FCSTD DOCUMENT  (FreeCAD 0.19R24291 (Git))
Label: P11 isometric
License: All rights reserved
LicenseURL: http://en.wikipedia.org/wiki/All_rights_reserved
objects: Part::Part2DObjectPython×25, App::FeaturePython×9
note: 25 computed .brp shape members not serialized (recipe doc carries the construction recipe); baked Part::Feature solids carry a one-line shape summary decoded from their .brp

FEATURE [Part::Part2DObjectPython] Line001  # Draft 2D object (typed FeaturePython)
  Area = 0
  ChamferSize = 0
  Closed = false
  End = (-15,0,0)
  FilletRadius = 0
  Length = 22.9544
  MakeFace = false
  Points = (2) [(7.95439,0,0),(-15,0,0)]
  Start = (7.95439,0,0)
  Subdivisions = 0
FEATURE [Part::Part2DObjectPython] Line003  # Draft 2D object (typed FeaturePython)
  Area = 0
  ChamferSize = 0
  Closed = false
  End = (-7.07107,7.07107,0)
  FilletRadius = 0
  Length = 10
  MakeFace = false
  Points = (2) [(0,0,0),(-7.07107,7.07107,0)]
  Start = (0,0,0)
  Subdivisions = 0
FEATURE [Part::Part2DObjectPython] Line004  # Draft 2D object (typed FeaturePython)
  Area = 0
  ChamferSize = 0
  Closed = false
  End = (-29.1421,14.1421,0)
  FilletRadius = 0
  Length = 20
  MakeFace = false
  Placement = pos=(-15,-1e-15,0) rot=(0,0,1;0rad)
  Points = (2) [(0,0,0),(-14.1421,14.1421,0)]
  Start = (-15,-1e-15,0)
  Subdivisions = 0
FEATURE [Part::Part2DObjectPython] Line005  # Draft 2D object (typed FeaturePython)
  Area = 0
  ChamferSize = 0
  Closed = false
  End = (-19.1421,14.1421,0)
  FilletRadius = 0
  Length = 10
  MakeFace = false
  Placement = pos=(-29.1421,14.1421,0) rot=(0,0,1;0rad)
  Points = (2) [(0,0,0),(10,-1.24345e-14,0)]
  Start = (-29.1421,14.1421,0)
  Subdivisions = 0
FEATURE [Part::Part2DObjectPython] Line006  # Draft 2D object (typed FeaturePython)
  Area = 0
  ChamferSize = 0
  Closed = false
  End = (-12.0711,7.07107,0)
  FilletRadius = 0
  Length = 10
  MakeFace = false
  Placement = pos=(-19.1421,14.1421,0) rot=(0,0,1;0rad)
  Points = (2) [(0,0,0),(7.07107,-7.07107,0)]
  Start = (-19.1421,14.1421,0)
  Subdivisions = 0
FEATURE [Part::Part2DObjectPython] Line008  # Draft 2D object (typed FeaturePython)
  Area = 0
  ChamferSize = 0
  Closed = false
  End = (-29.1421,44.1421,0)
  FilletRadius = 0
  Length = 30
  MakeFace = false
  Placement = pos=(-29.1421,14.1421,0) rot=(0,0,1;0rad)
  Points = (2) [(0,0,0),(0,30,0)]
  Start = (-29.1421,14.1421,0)
  Subdivisions = 0
FEATURE [Part::Part2DObjectPython] Line009  # Draft 2D object (typed FeaturePython)
  Area = 0
  ChamferSize = 0
  Closed = false
  End = (-19.1421,44.1421,0)
  FilletRadius = 0
  Length = 30
  MakeFace = false
  Points = (2) [(-19.1421,14.1421,0),(-19.1421,44.1421,0)]
  Start = (-19.1421,14.1421,0)
  Subdivisions = 0
FEATURE [Part::Part2DObjectPython] Line011  # Draft 2D object (typed FeaturePython)
  Area = 0
  ChamferSize = 0
  Closed = false
  End = (-12.0711,37.0711,0)
  FilletRadius = 0
  Length = 30
  MakeFace = false
  Placement = pos=(-12.0711,7.07107,0) rot=(0,0,1;0rad)
  Points = (2) [(0,0,0),(1.77636e-15,30,0)]
  Start = (-12.0711,7.07107,0)
  Subdivisions = 0
FEATURE [Part::Part2DObjectPython] Line014  # Draft 2D object (typed FeaturePython)
  Area = 0
  ChamferSize = 0
  Closed = false
  End = (-12.0711,37.0711,0)
  FilletRadius = 0
  Length = 5
  MakeFace = false
  Points = (2) [(-7.07107,37.0711,0),(-12.0711,37.0711,0)]
  Start = (-7.07107,37.0711,0)
  Subdivisions = 0
FEATURE [Part::Part2DObjectPython] Line017  # Draft 2D object (typed FeaturePython)
  Area = 0
  ChamferSize = 0
  Closed = false
  End = (0,15,0)
  FilletRadius = 0
  Length = 10
  MakeFace = false
  Placement = pos=(-7.07107,22.0711,0) rot=(0,0,1;0rad)
  Points = (2) [(0,0,0),(7.07107,-7.07107,0)]
  Start = (-7.07107,22.0711,0)
  Subdivisions = 0
FEATURE [Part::Part2DObjectPython] Line018  # Draft 2D object (typed FeaturePython)
  Area = 0
  ChamferSize = 0
  Closed = false
  End = (-7.07107,7.07107,0)
  FilletRadius = 0
  Length = 5
  MakeFace = false
  Placement = pos=(-12.0711,7.07107,0) rot=(0,0,1;0rad)
  Points = (2) [(0,0,0),(5,1.86517e-14,0)]
  Start = (-12.0711,7.07107,0)
  Subdivisions = 0
FEATURE [Part::Part2DObjectPython] Line020  # Draft 2D object (typed FeaturePython)
  Area = 0
  ChamferSize = 0
  Closed = false
  End = (-7.07107,22.0711,0)
  FilletRadius = 0
  Length = 15
  MakeFace = false
  Placement = pos=(-7.07107,7.07107,0) rot=(0,0,1;0rad)
  Points = (2) [(0,0,0),(-5.50671e-14,15,0)]
  Start = (-7.07107,7.07107,0)
  Subdivisions = 0
FEATURE [Part::Part2DObjectPython] Line023  # Draft 2D object (typed FeaturePython)
  Area = 0
  ChamferSize = 0
  Closed = false
  End = (0,15,0)
  FilletRadius = 0
  Length = 10
  MakeFace = false
  Placement = pos=(0,15,0) rot=(0,0,1;0rad)
  Points = (2) [(10,0,0),(0,0,0)]
  Start = (10,15,0)
  Subdivisions = 0
FEATURE [Part::Part2DObjectPython] Line024  # Draft 2D object (typed FeaturePython)
  Area = 0
  ChamferSize = 0
  Closed = false
  End = (2.92893,22.0711,0)
  FilletRadius = 0
  Length = 10
  MakeFace = false
  Placement = pos=(10,15,0) rot=(0,0,1;0rad)
  Points = (2) [(0,0,0),(-7.07107,7.07107,0)]
  Start = (10,15,0)
  Subdivisions = 0
FEATURE [Part::Part2DObjectPython] Line026  # Draft 2D object (typed FeaturePython)
  Area = 0
  ChamferSize = 0
  Closed = false
  End = (-7.07107,22.0711,0)
  FilletRadius = 0
  Length = 10
  MakeFace = false
  Placement = pos=(2.92893,22.0711,0) rot=(0,0,1;0rad)
  Points = (2) [(0,0,0),(-10,0,0)]
  Start = (2.92893,22.0711,0)
  Subdivisions = 0
FEATURE [Part::Part2DObjectPython] Line028  # Draft 2D object (typed FeaturePython)
  Area = 0
  ChamferSize = 0
  Closed = false
  End = (2.92893,37.0711,0)
  FilletRadius = 0
  Length = 15
  MakeFace = false
  Points = (2) [(2.92893,22.0711,0),(2.92893,37.0711,0)]
  Start = (2.92893,22.0711,0)
  Subdivisions = 0
FEATURE [Part::Part2DObjectPython] Line029  # Draft 2D object (typed FeaturePython)
  Area = 0
  ChamferSize = 0
  Closed = false
  End = (2.92893,37.0711,0)
  FilletRadius = 0
  Length = 10
  MakeFace = false
  Placement = pos=(-7.07107,37.0711,0) rot=(0,0,1;0rad)
  Points = (2) [(0,0,0),(10,3.55271e-14,0)]
  Start = (-7.07107,37.0711,0)
  Subdivisions = 0
FEATURE [Part::Part2DObjectPython] Line030  # Draft 2D object (typed FeaturePython)
  Area = 0
  ChamferSize = 0
  Closed = false
  End = (10,30,0)
  FilletRadius = 0
  Length = 10
  MakeFace = false
  Placement = pos=(2.92893,37.0711,0) rot=(0,0,1;0rad)
  Points = (2) [(0,0,0),(7.07107,-7.07107,0)]
  Start = (2.92893,37.0711,0)
  Subdivisions = 0
FEATURE [Part::Part2DObjectPython] Line031  # Draft 2D object (typed FeaturePython)
  Area = 0
  ChamferSize = 0
  Closed = false
  End = (10,15,0)
  FilletRadius = 0
  Length = 15
  MakeFace = false
  Placement = pos=(10,30,0) rot=(0,0,1;0rad)
  Points = (2) [(0,0,0),(-7.10543e-15,-15,0)]
  Start = (10,30,0)
  Subdivisions = 0
FEATURE [Part::Part2DObjectPython] Line032  # Draft 2D object (typed FeaturePython)
  Area = 0
  ChamferSize = 0
  Closed = false
  End = (-19.1421,44.1421,0)
  FilletRadius = 0
  Length = 10
  MakeFace = false
  Placement = pos=(-29.1421,44.1421,0) rot=(0,0,1;0rad)
  Points = (2) [(0,0,0),(10,0,0)]
  Start = (-29.1421,44.1421,0)
  Subdivisions = 0
FEATURE [Part::Part2DObjectPython] Line033  # Draft 2D object (typed FeaturePython)
  Area = 0
  ChamferSize = 0
  Closed = false
  End = (-12.0711,37.0711,0)
  FilletRadius = 0
  Length = 10
  MakeFace = false
  Placement = pos=(-19.1421,44.1421,0) rot=(0,0,1;0rad)
  Points = (2) [(0,0,0),(7.07107,-7.07107,0)]
  Start = (-19.1421,44.1421,0)
  Subdivisions = 0
FEATURE [Part::Part2DObjectPython] Line  # Draft 2D object (typed FeaturePython)
  Area = 0
  ChamferSize = 0
  Closed = false
  End = (0,15,0)
  FilletRadius = 0
  Length = 15
  MakeFace = false
  Points = (2) [(0,0,0),(4.59243e-16,15,0)]
  Start = (0,0,0)
  Subdivisions = 0
FEATURE [App::FeaturePython] Dimension  # Draft dimension (typed FeaturePython)
  Diameter = false
  Dimline = (0,-3,0)
  Direction = (0,0,0)
  Distance = 15
  End = (0,0,0)
  Normal = (0,0,1)
  Start = (-15,0,0)
FEATURE [App::FeaturePython] Dimension002  # Draft dimension (typed FeaturePython)
  Diameter = false
  Dimline = (-29.1421,11.1421,0)
  Direction = (0,0,0)
  Distance = 20
  End = (-29.1421,14.1421,0)
  Normal = (0,0,1)
  Start = (-15,-1e-15,0)
FEATURE [App::FeaturePython] Dimension003  # Draft dimension (typed FeaturePython)
  Diameter = false
  Dimline = (-19.1421,47.1421,0)
  Direction = (0,0,0)
  Distance = 10
  End = (-19.1421,44.1421,0)
  Normal = (0,0,1)
  Start = (-29.1421,44.1421,0)
FEATURE [App::FeaturePython] Dimension004  # Draft dimension (typed FeaturePython)
  Diameter = false
  Dimline = (12.185,32.185,0)
  Direction = (0,0,0)
  Distance = 10
  End = (10,30,0)
  Normal = (0,0,1)
  Start = (2.92893,37.0711,0)
FEATURE [Part::Part2DObjectPython] Line034  # Draft 2D object (typed FeaturePython)
  Area = 0
  ChamferSize = 0
  Closed = false
  End = (-7.07107,7.07107,0)
  FilletRadius = 0
  Length = 30
  MakeFace = false
  Placement = pos=(-7.07107,7.07107,0) rot=(0,0,1;0rad)
  Points = (2) [(-1.08358e-13,30,0),(0,-8.88178e-16,0)]
  Start = (-7.07107,37.0711,0)
  Subdivisions = 0
FEATURE [App::FeaturePython] Dimension005  # Draft dimension (typed FeaturePython)
  Diameter = false
  Dimline = (0.527457,28.2446,0)
  Direction = (0,0,0)
  Distance = 10
  End = (2.92893,22.0711,0)
  Normal = (0,0,1)
  Start = (-7.07107,22.0711,0)
FEATURE [App::FeaturePython] Dimension006  # Draft dimension (typed FeaturePython)
  Diameter = false
  Dimline = (14.2416,0.758433,0)
  Direction = (0,0,0)
  Distance = 15
  End = (0,15,0)
  Normal = (0,0,1)
  Start = (0,0,0)
FEATURE [App::FeaturePython] Dimension007  # Draft dimension (typed FeaturePython)
  Diameter = false
  Dimline = (19.7719,22.161,0)
  Direction = (0,0,0)
  Distance = 30
  End = (10,30,0)
  Normal = (0,0,1)
  Start = (10,0,0)
FEATURE [App::FeaturePython] Dimension008  # Draft dimension (typed FeaturePython)
  Diameter = false
  Dimline = (6.00669,-8.1373,0)
  Direction = (0,0,0)
  Distance = 22.9544
  End = (7.95439,0,0)
  Normal = (0,0,1)
  Start = (-15,0,0)
FEATURE [Part::Part2DObjectPython] Line036  # Draft 2D object (typed FeaturePython)
  Area = 0
  ChamferSize = 0
  Closed = false
  End = (2.92893,37.0711,0)
  FilletRadius = 0
  Length = 15
  MakeFace = false
  Placement = pos=(2.92893,22.0711,0) rot=(0,0,1;0rad)
  Points = (2) [(0,0,0),(-1.12799e-13,15,0)]
  Start = (2.92893,22.0711,0)
  Subdivisions = 0
FEATURE [Part::Part2DObjectPython] Line037  # Draft 2D object (typed FeaturePython)
  Area = 0
  ChamferSize = 0
  Closed = false
  End = (2.92893,37.0711,0)
  FilletRadius = 0
  Length = 15
  MakeFace = false
  Placement = pos=(2.92893,22.0711,0) rot=(0,0,1;0rad)
  Points = (2) [(0,0,0),(-1.12799e-13,15,0)]
  Start = (2.92893,22.0711,0)
  Subdivisions = 0
FEATURE [App::FeaturePython] Text  # WARN: FeaturePython — macro-defined, semantics opaque (R4)
  Placement = pos=(20.1825,-23.0473,0) rot=(0,0,1;0rad)
  Text = All Dimensions are in mm
